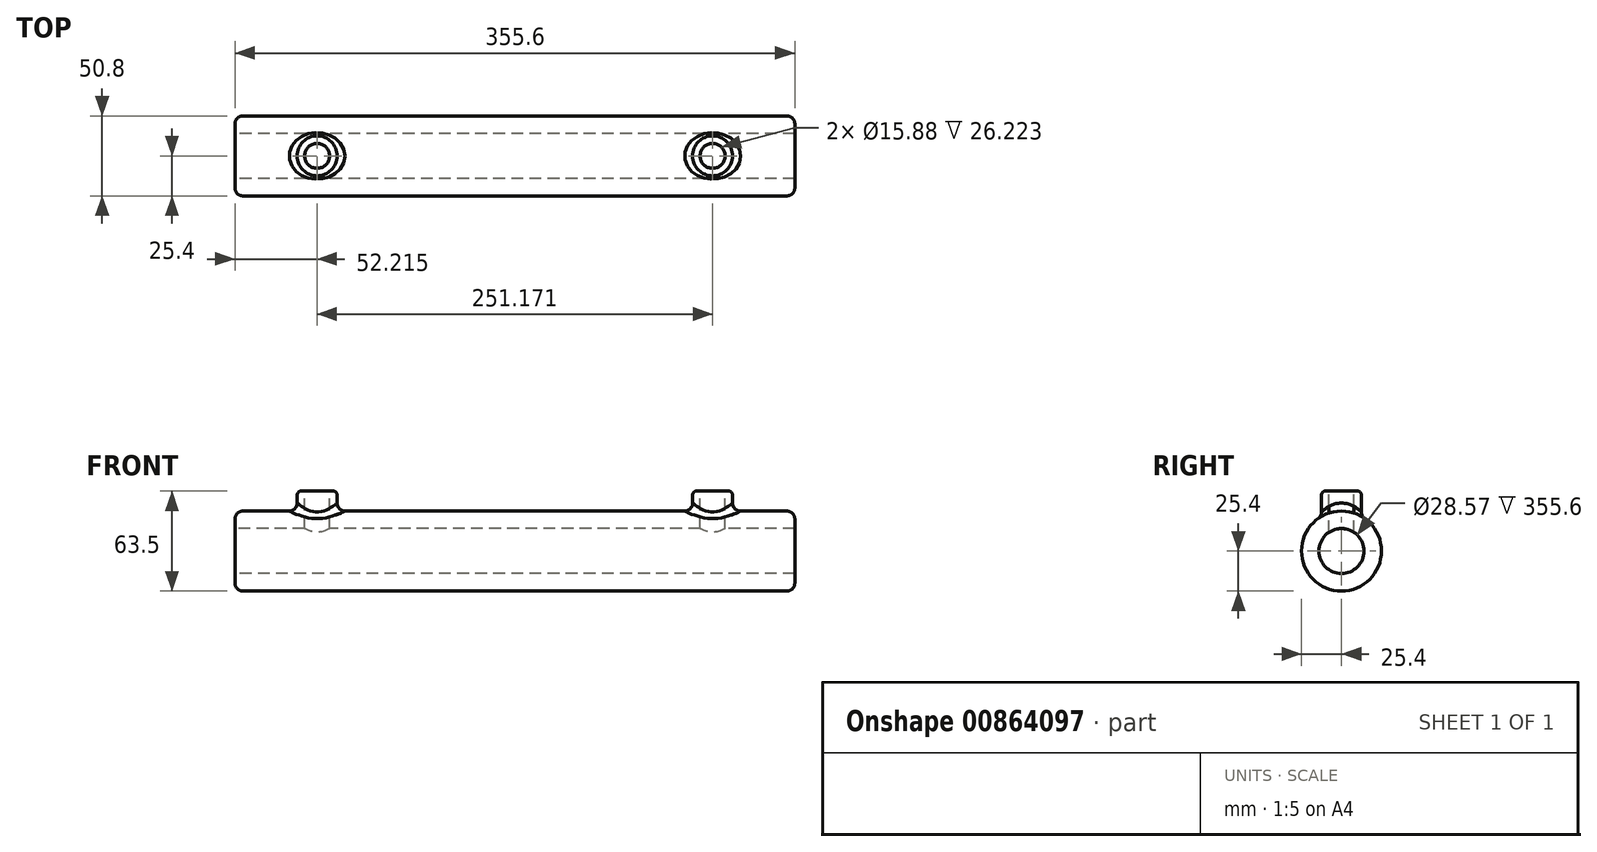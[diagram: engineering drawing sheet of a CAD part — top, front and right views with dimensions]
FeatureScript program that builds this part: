
annotation { "Feature Type Name" : "Feature", "Feature Type Description" : "" }
export const myFeature = defineFeature(function(context is Context, id is Id, definition is map)
    precondition{}
    {
        {
            var Q0;
            Q0=qCreatedBy(makeId("Right.planeOp"),FACE);
            var sketch = newSketch(context, id + "F0", { "sketchPlane" : qUnion([Q0])});
            skCircle(sketch, "E0", {"center": v(0, 0) * mm, "radius": 25.4 * mm});
            skSolve(sketch);
        }
        {
            var Q0;
            Q0=makeQuery(id+"F0.imprint","IMPRINT",FACE,{"disambiguationData":[TD([[makeQuery(id+"F0.imprint","IMPRINT",EDGE,{"derivedFrom":sQuery(id+"F0.wireOp",EDGE,"E0")}),1.0]])]});
            extrude(context, id + "F1", {"entities" : qUnion([Q0]), "depth" : 355.6 * mm, "offsetDistance" : 25.4 * mm, "symmetric" : true});
        }
        {
            var Q0;
            Q0=qCreatedBy(makeId("Top.planeOp"),FACE);
            var sketch = newSketch(context, id + "F2", { "sketchPlane" : qUnion([Q0])});
            skCircle(sketch, "E1", {"center": v(-125.59, 0) * mm, "radius": 12.7 * mm});
            skCircle(sketch, "E2.MirrorC", {"center": v(125.59, 0) * mm, "radius": 12.7 * mm});
            skSolve(sketch);
        }
        {
            var Q0;
            Q0 = qSketchRegion(id + "F2", true);
            extrude(context, id + "F3", {"entities" : qUnion([Q0]), "operationType" : NewBodyOperationType.ADD, "depth" : 38.1 * mm, "offsetDistance" : 25.4 * mm});
        }
        {
            var Q0;
            Q0=makeQuery(id+"F3.opExtrude","CAP_FACE",FACE,{"disambiguationData":[OSD([sQuery(id+"F2.wireOp",EDGE,"E1")])],"isStart":false});
            var sketch = newSketch(context, id + "F4", { "sketchPlane" : qUnion([Q0])});
            skCircle(sketch, "E3", {"center": v(-125.59, 0) * mm, "radius": 7.94 * mm});
            skSolve(sketch);
        }
        {
            var Q0;
            Q0=makeQuery(id+"F3.opExtrude","CAP_FACE",FACE,{"disambiguationData":[OSD([sQuery(id+"F2.wireOp",EDGE,"E2.MirrorC")])],"isStart":false});
            var sketch = newSketch(context, id + "F5", { "sketchPlane" : qUnion([Q0])});
            skCircle(sketch, "E4", {"center": v(125.59, 0) * mm, "radius": 7.94 * mm});
            skSolve(sketch);
        }
        {
            var Q0;
            Q0=makeQuery(id+"F5.imprint","IMPRINT",FACE,{"disambiguationData":[TD([[makeQuery(id+"F5.imprint","IMPRINT",EDGE,{"derivedFrom":sQuery(id+"F5.wireOp",EDGE,"E4")}),1.0]])]});
            var Q1;
            Q1=makeQuery(id+"F4.imprint","IMPRINT",FACE,{"disambiguationData":[TD([[makeQuery(id+"F4.imprint","IMPRINT",EDGE,{"derivedFrom":sQuery(id+"F4.wireOp",EDGE,"E3")}),1.0]])]});
            extrude(context, id + "F6", {"entities" : qUnion([Q0, Q1]), "operationType" : NewBodyOperationType.REMOVE, "oppositeDirection" : true, "depth" : 38.1 * mm, "offsetDistance" : 25.4 * mm});
        }
        {
            var Q0;
            Q0=makeQuery(id+"F1.opExtrude","CAP_FACE",FACE,{"disambiguationData":[OSD([sQuery(id+"F0.wireOp",EDGE,"E0")])],"isStart":true});
            var sketch = newSketch(context, id + "F7", { "sketchPlane" : qUnion([Q0])});
            skCircle(sketch, "E5", {"center": v(0, 0) * mm, "radius": 14.29 * mm});
            skSolve(sketch);
        }
        {
            var Q0;
            Q0=makeQuery(id+"F7.imprint","IMPRINT",FACE,{"disambiguationData":[TD([[makeQuery(id+"F7.imprint","IMPRINT",EDGE,{"derivedFrom":sQuery(id+"F7.wireOp",EDGE,"E5")}),1.0]])]});
            extrude(context, id + "F8", {"entities" : qUnion([Q0]), "operationType" : NewBodyOperationType.REMOVE, "endBound" : BoundingType.THROUGH_ALL, "oppositeDirection" : true, "depth" : 25.4 * mm, "offsetDistance" : 25.4 * mm});
        }
        {
            var Q0;
            Q0=makeQuery(id+"F1.opExtrude","CAP_EDGE",EDGE,{"disambiguationData":[OSD([sQuery(id+"F0.wireOp",EDGE,"E0")])],"isStart":true});
            var Q1;
            Q1=makeQuery(id+"F1.opExtrude","CAP_EDGE",EDGE,{"disambiguationData":[OSD([sQuery(id+"F0.wireOp",EDGE,"E0")])],"isStart":false});
            fillet(context, id + "F9", {"entities" : qUnion([Q0, Q1]), "radius" : 5.08 * mm, "tangentPropagation" : true, "allowEdgeOverflow" : false});
        }
        {
            var Q0;
            Q0=makeQuery(id+"F3.boolean.opBoolean","INTERSECT",EDGE,{"derivedFrom":[makeQuery(id+"F1.opExtrude","SWEPT_FACE",FACE,{"disambiguationData":[OSD([sQuery(id+"F0.wireOp",EDGE,"E0")])]}),makeQuery(id+"F3.opExtrude","SWEPT_FACE",FACE,{"disambiguationData":[OSD([sQuery(id+"F2.wireOp",EDGE,"E1")])]})]});
            var Q1;
            Q1=makeQuery(id+"F3.boolean.opBoolean","INTERSECT",EDGE,{"derivedFrom":[makeQuery(id+"F1.opExtrude","SWEPT_FACE",FACE,{"disambiguationData":[OSD([sQuery(id+"F0.wireOp",EDGE,"E0")])]}),makeQuery(id+"F3.opExtrude","SWEPT_FACE",FACE,{"disambiguationData":[OSD([sQuery(id+"F2.wireOp",EDGE,"E2.MirrorC")])]})]});
            fillet(context, id + "F10", {"entities" : qUnion([Q0, Q1]), "radius" : 5.08 * mm, "tangentPropagation" : true, "allowEdgeOverflow" : false});
        }
        {
            var Q0;
            Q0=makeQuery(id+"F3.opExtrude","CAP_EDGE",EDGE,{"disambiguationData":[OSD([sQuery(id+"F2.wireOp",EDGE,"E1")])],"isStart":false});
            var Q1;
            Q1=makeQuery(id+"F3.opExtrude","CAP_EDGE",EDGE,{"disambiguationData":[OSD([sQuery(id+"F2.wireOp",EDGE,"E2.MirrorC")])],"isStart":false});
            fillet(context, id + "F11", {"entities" : qUnion([Q0, Q1]), "radius" : 2.54 * mm, "tangentPropagation" : true, "allowEdgeOverflow" : false});
        }
    });
